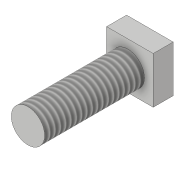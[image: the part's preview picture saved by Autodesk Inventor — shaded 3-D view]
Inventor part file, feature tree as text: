
AUTODESK INVENTOR PART (.ipt)
format: ipt  version: 2019 (Build 230136000, 136)  size: 92,160 bytes
history: native  units: in
note: dims shown in document units (in); Inventor stores cm internally (conversion verified against a paired STEP export)
features: extrude x2, sketch x2, thread x1
ambient origin geometry x8: Origin, YZ Plane, XZ Plane, XY Plane, X Axis, Y Axis, Z Axis, Center Point
bodies: Solid1 (feature_tree)
feature tree (5):
  extrude  "Extrusion1"  Depth=0.2756in
  extrude  "Extrusion2"  Depth=0.3937in
  thread  "Thread1"  [1 undecoded]
  sketch  "Sketch1"  dims[d0=0.2756in d1=0.2756in]
  sketch  "Sketch2"  dims[d2=0.1181in d3=0.0in d4=0.1969in d5=0.5906in d6=0.0in d7=0.3937in d8=0.0in]
note: 1 required parameter value undecoded (feature->parameter linkage not recoverable at this tier; creation-order binding heuristic only, values carry confidence <= 0.55)
